# Revit family: HVAC_Mechanical-Ventilation_Ice-Air_FCU_Horizontal-Concealed-Ultra-Thin
name_source: partatom
category: Mechanical Equipment
revit_build: Autodesk Revit 2015 (Build: 20140606_1530(x64)
units: mm (PartAtom-declared; Revit-internal decimal feet)

## types (4) — shared parameters
Air Supply Height = 4.75 "
Aluminum Material = Aluminum - Ice_Air - White
BIMobject category = Air Conditioning
BIMobject category code = hvac-air-con
BIMobject main category = HVAC
BIMobject main category code = hvac
Brand url = http://www.ice-air.com
Condensate Connection = 0.63 "
Copper Material = Copper - Ice_Air - Orange
Default Elevation = 48 "
Depth = 19.33 "
Description = Easily adaptable for concealed or above-ceiling mounting, the FCHC compact fan coil units save floor
space, making it an ideal choice for use in new construction and retrofit applications.
Design country = United States
Duct Description = Supply Air
Edition number = 1
Frequency = 60 Hz
Height = 8 "
IFC Classification = Heat Exchanger
Inlet/Outlet Connection = 0.5 "
Manufacturer = Ice Air
Manufacturer country = United States
Manufacturer name = Ice Air
Masterformat 2014 Code = 23 82 19
Masterformat 2014 Description = Fan Coil Units
Motor = 115V/60Hz
NBS Reference Code = 65-00-29
NBS Reference Description = Fan Coil Units
OmniClass Code = 23-33 33 11
OmniClass Description = Fan Coil Units
Product Guid = dd888e62-749f-45f2-abef-a9e304967da1
Product SKU = horizontal-concealed-ultra-thin-fcu
Product data url = https://bimobject.com
Product family = FCU
Product group = Horizontal Concealed Ultra Thin
Product url = http://www.ice-air.com
QR code = http://bimobject.com
Steel Material = Steel - Ice_Air - Galvanized
Technical description = http://www.ice-air.com
UNSPSC Code = 4010
URL = http://www.ice-air.com
Uniclass 1.4 Code = JU84
Uniclass 1.4 Description = Heating and cooling coils
Uniclass 2.0 Code = PR-65-00-29
Uniclass 2.0 Description = Fan Coil Units
Uniclass 2015 Code = Pr_60_65_37
Uniclass 2015 Name = Heating and cooling coils
Uniformat II Code = D3090
Uniformat II Description = Other HVAC Systems & Equipment
Voltage = 115 V
Weight Net (Kg) = 0
z 2-pipe = Pipe System : 2-pipe
z 4-pipe = Pipe System : 4-pipe
zero-valued in all types: Nominal height, Nominal width

## per-type parameters (varying)
| type | 1 vent | 2 vent | Air Flow (High) | Air Flow (Low) | Air Flow (Med) | Air Supply Width | Cooling Capacity (High) | Cooling Capacity (Low) | Cooling Capacity (Med) | Drain Connection Offset | Duct Box Width | Heating Capacity (High) | Heating Capacity (Low) | Heating Capacity (Med) | Type 1 Vis | Type 3 Vis | Type 4 Vis | Vent Gap | Width | z Type |
| 5FCHCU02 | Yes | No | 200 CFM | 100 CFM | 150 CFM | 18 " | 4900.0 Btu/h | 2940.0 Btu/h | 3675.0 Btu/h | 18.52 " | 20.38 " | 8300.0 Btu/h | 4980.0 Btu/h | 6225.0 Btu/h | Yes | No | No | 11.15 " | 30.31 " | 1 |
| 5FCHCU03 | Yes | No | 300 CFM | 150 CFM | 225 CFM | 18 " | 7000.0 Btu/h | 4200.0 Btu/h | 5250.0 Btu/h | 18.52 " | 20.38 " | 11600.0 Btu/h | 6960.0 Btu/h | 8700.0 Btu/h | Yes | No | No | 11.15 " | 30.31 " | 2 |
| 5FCHCU04 | No | Yes | 400 CFM | 200 CFM | 300 CFM | 28 " | 11900.0 Btu/h | 7140.0 Btu/h | 8925.0 Btu/h | 25.84 " | 29.38 " | 19600.0 Btu/h | 11760.0 Btu/h | 14700.0 Btu/h | No | Yes | No | 3.45 " | 42.13 " | 3 |
| 5FCHCU06 | No | Yes | 600 CFM | 300 CFM | 450 CFM | 32 " | 15300.0 Btu/h | 9180.0 Btu/h | 11475.0 Btu/h | 27.65 " | 33.63 " | 26700.0 Btu/h | 16020.0 Btu/h | 20025.0 Btu/h | No | No | Yes | 3.45 " | 46.06 " | 4 |

note: column(s) folded — value = type name in every type: Model

## geometry (parser evidence)
native form markers: Sweep x3
no freeform markers — native parametric forms only
